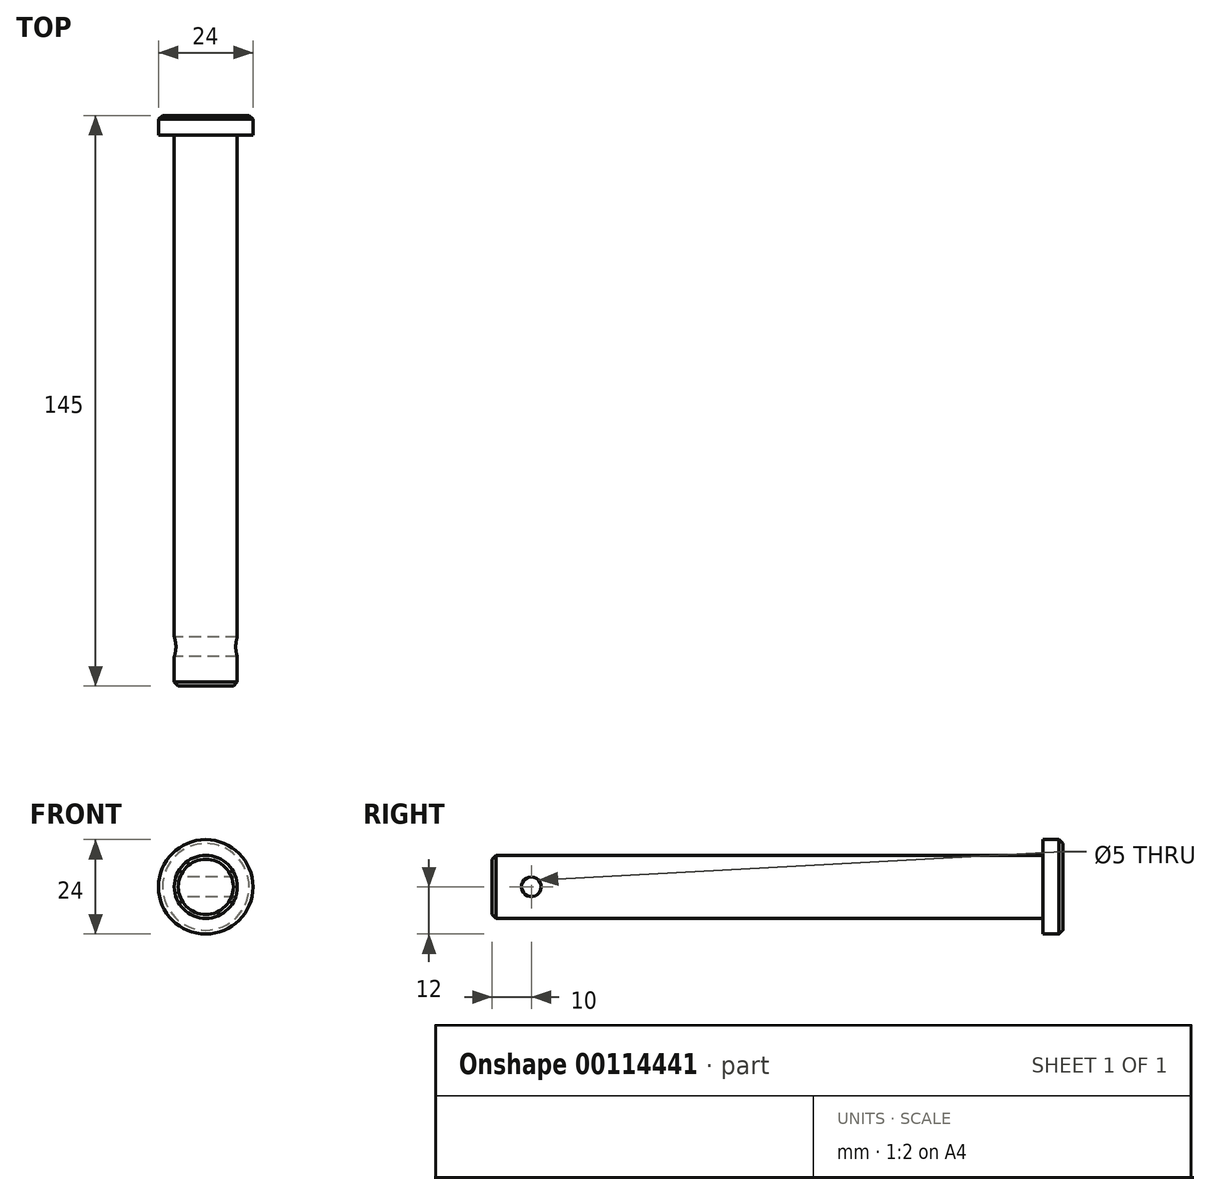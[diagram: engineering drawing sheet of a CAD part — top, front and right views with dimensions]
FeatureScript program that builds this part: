
annotation { "Feature Type Name" : "Feature", "Feature Type Description" : "" }
export const myFeature = defineFeature(function(context is Context, id is Id, definition is map)
    precondition{}
    {
        {
            var Q0;
            Q0=qCreatedBy(makeId("Front.planeOp"),FACE);
            var sketch = newSketch(context, id + "F0", { "sketchPlane" : qUnion([Q0])});
            skCircle(sketch, "E0", {"center": v(0, 0) * mm, "radius": 8 * mm});
            skCircle(sketch, "E1", {"center": v(0, 0) * mm, "radius": 12 * mm});
            skSolve(sketch);
        }
        {
            var Q0;
            Q0=makeQuery(id+"F0.imprint","IMPRINT",FACE,{"disambiguationData":[TD([[makeQuery(id+"F0.imprint","IMPRINT",EDGE,{"derivedFrom":sQuery(id+"F0.wireOp",EDGE,"E0")}),1.0]])]});
            extrude(context, id + "F1", {"entities" : qUnion([Q0]), "depth" : 140 * mm});
        }
        {
            var Q0;
            Q0=makeQuery(id+"F0.imprint","IMPRINT",FACE,{"disambiguationData":[TD([[makeQuery(id+"F0.imprint","IMPRINT",EDGE,{"derivedFrom":sQuery(id+"F0.wireOp",EDGE,"E0")}),-1.0]])]});
            var Q1;
            Q1=makeQuery(id+"F0.imprint","IMPRINT",FACE,{"disambiguationData":[TD([[makeQuery(id+"F0.imprint","IMPRINT",EDGE,{"derivedFrom":sQuery(id+"F0.wireOp",EDGE,"E0")}),1.0]])]});
            extrude(context, id + "F2", {"entities" : qUnion([Q0, Q1]), "operationType" : NewBodyOperationType.ADD, "oppositeDirection" : true, "depth" : 5 * mm});
        }
        {
            var Q0;
            Q0=makeQuery(id+"F2.opExtrude","CAP_EDGE",EDGE,{"disambiguationData":[OSD([sQuery(id+"F0.wireOp",EDGE,"E1")])],"isStart":false});
            var Q1;
            Q1=makeQuery(id+"F1.opExtrude","CAP_EDGE",EDGE,{"disambiguationData":[OSD([sQuery(id+"F0.wireOp",EDGE,"E0")])],"isStart":false});
            chamfer(context, id + "F3", {"entities" : qUnion([Q0, Q1]), "width" : 1 * mm, "tangentPropagation" : true});
        }
        {
            var Q0;
            Q0=qCreatedBy(makeId("Right.planeOp"),FACE);
            cPlane(context, id + "F4", {"entities" : qUnion([Q0]), "cplaneType" : CPlaneType.OFFSET, "offset" : 8 * mm, "oppositeDirection" : true, "width" : 150 * mm, "height" : 150 * mm});
        }
        {
            var Q0;
            Q0=qCreatedBy(id+"F4.planeOp",FACE);
            var sketch = newSketch(context, id + "F5", { "sketchPlane" : qUnion([Q0])});
            skCircle(sketch, "E2", {"center": v(-130, 0) * mm, "radius": 2.5 * mm});
            skSolve(sketch);
        }
        {
            var Q0;
            Q0=makeQuery(id+"F5.imprint","IMPRINT",FACE,{"disambiguationData":[TD([[makeQuery(id+"F5.imprint","IMPRINT",EDGE,{"derivedFrom":sQuery(id+"F5.wireOp",EDGE,"E2")}),1.0]])]});
            extrude(context, id + "F6", {"entities" : qUnion([Q0]), "operationType" : NewBodyOperationType.REMOVE, "endBound" : BoundingType.THROUGH_ALL, "depth" : 25 * mm});
        }
    });
